# Revit family: Steel-TFB Tapered Flange Beam-Steel & Tube-350
name_source: partatom
category: Structural Framing
revit_build: Autodesk Revit 2017 (Build: 20170118_1100(x64)
units: mm (PartAtom-declared; Revit-internal decimal feet)

## family parameters
Always export as geometry = No
Always vertical = Yes
Cut with Voids When Loaded = No
Material for Model Behavior = Steel
OmniClass Number = 23.25.30.11.14.14
OmniClass Title = Beams
Section Shape = I-shape Sloped Flange
Shared = No
Show family pre-cut in plan views = Yes
Structural Framing Length Roundoff = 0 mm

## types (2) — shared parameters
Assembly Code = B1020230
CBICode = 3421
CBIDescription = Light steel framing
Description = Steel & Tube supplies a full range of hot rolled seismic and non seismic universal beams, columns, plate and channels. For more information please refer to the Design with Steel product catalogue on our website.
Design Instruction = Design information should be cross referenced with the Steel & Tube Design with Steel Design Guide and NZS 3404: Part1: 2009
Design Standard = NZS 3404: Part 1: 2009 including reference to the NZBC
Form Factor = 1
Manufactured Standard = AS/NZS 3679.1: 2016
Manufacturer = Steel & Tube
ManufacturerName = Steel & Tube
ManufacturerURL = http://www.steelandtube.co.nz
MaximumLength_ANZRS = 16500 mm  [stored 54.1339 ft]
ModifiedIssue_ANZRS = 20160329.01 $
Principal Axes Angle = 90.00°
Tensile Strength = 480.0 MPa
Torsional Modulus = 0.0 mm³
URL = http://www.steelandtube.co.nz
Uniclass2015Code = Pr_20_76_51_12
Uniclass2015Title = Carbon steel beams, columns, channels and tees
Uniclass2015Version = 2015
X-Compactness = C
Y-Compactness = C
Yield Stress Flange = 360.0 MPa
Yield Stress Web = 360.0 MPa

## per-type parameters (varying)
- TFB125: Centroid Horizontal=32.5 mm; Centroid Vertical=62.5 mm; Clear Web Height=109.0 mm; Elastic Modulus strong axis=80300.0 mm³; Elastic Modulus weak axis=17200.0 mm³; Flange Fillet=4.0 mm; Flange Thickness=8.5 mm; Flange Toe of Fillet=10.5 mm; Height=125.0 mm; MassPerUnitLength_ANZRS=13.10 kg/m; Model=125TFB; Moment of Inertia strong axis=4340000.00 mm4; Moment of Inertia weak axis=337000.00 mm4; Nominal Weight=13.10 kgf/m; Perimeter=0.47 m²/m; Plastic Modulus strong axis=69400.0 mm³; Plastic Modulus weak axis=10400.0 mm³; Section Area=1670.0 mm²; Section Name Key=TFB 125; SectionAreaGross_ANZRS=1670.0 mm²; SectionAreaNet_ANZRS=1670.0 mm²; Shear Area strong axis=1670.0 mm²; Shear Area weak axis=1670.0 mm²; Torsional Moment of Inertia=40200.00 mm4; Warping Constant=1140000000.0 mm6; Web Fillet=8.0 mm; Web Thickness=5.0 mm; Web Toe of Fillet=22.0 mm; Width=65.0 mm; X-Zex=80300.0 mm³; Y-Zey=15600.0 mm³
- TFB100: Centroid Horizontal=22.5 mm; Centroid Vertical=50.0 mm; Clear Web Height=86.0 mm; Elastic Modulus strong axis=34100.0 mm³; Elastic Modulus weak axis=6000.0 mm³; Flange Fillet=3.0 mm; Flange Thickness=6.0 mm; Flange Toe of Fillet=9.0 mm; Height=100.0 mm; MassPerUnitLength_ANZRS=7.20 kg/m; Model=100TFB; Moment of Inertia strong axis=1460000.00 mm4; Moment of Inertia weak axis=79500.00 mm4; Nominal Weight=7.20 kgf/m; Perimeter=0.35 m²/m; Plastic Modulus strong axis=29200.0 mm³; Plastic Modulus weak axis=3530.0 mm³; Section Area=917.0 mm²; Section Name Key=TFB 100; SectionAreaGross_ANZRS=917.0 mm²; SectionAreaNet_ANZRS=917.0 mm²; Shear Area strong axis=917.0 mm²; Shear Area weak axis=917.0 mm²; Torsional Moment of Inertia=11600.00 mm4; Warping Constant=176000000.0 mm6; Web Fillet=7.0 mm; Web Thickness=4.0 mm; Web Toe of Fillet=13.5 mm; Width=45.0 mm; X-Zex=34100.0 mm³; Y-Zey=5300.0 mm³

note: [stored X ft] marks values corroborated as IEEE doubles in the binary element streams (Revit-internal decimal feet)

## geometry (parser evidence)
native form markers: Sweep x4
no freeform markers — native parametric forms only
